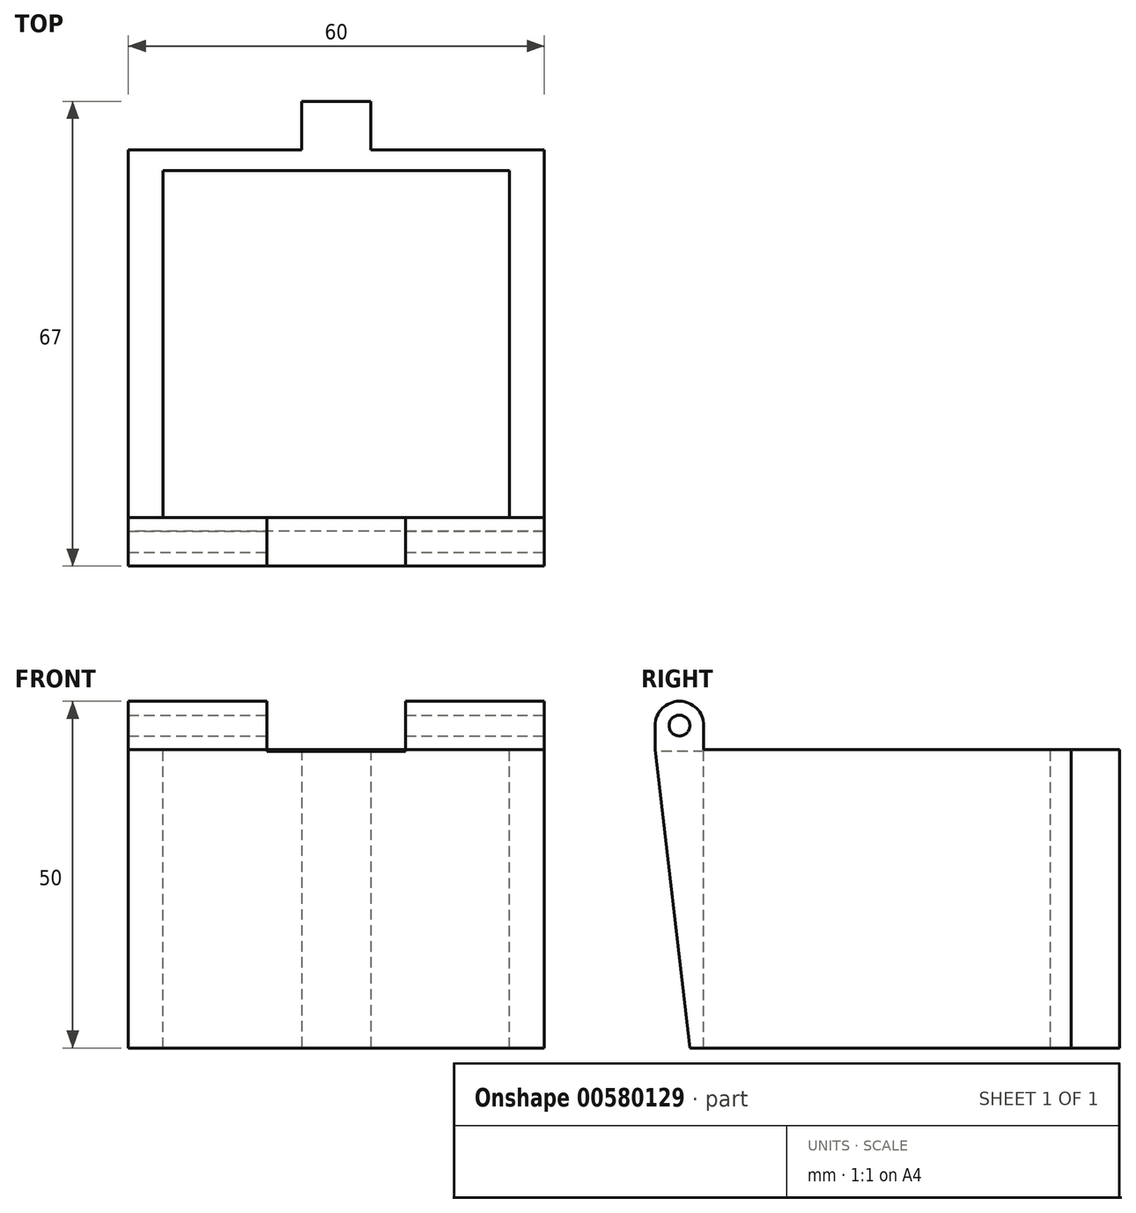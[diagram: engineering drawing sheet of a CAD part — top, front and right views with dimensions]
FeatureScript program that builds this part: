
annotation { "Feature Type Name" : "Feature", "Feature Type Description" : "" }
export const myFeature = defineFeature(function(context is Context, id is Id, definition is map)
    precondition{}
    {
        {
            var Q0;
            Q0=qCreatedBy(makeId("Top.planeOp"),FACE);
            var sketch = newSketch(context, id + "F0", { "sketchPlane" : qUnion([Q0])});
            skLineSegment(sketch, "E0.bottom", {"start": v(-57.5, 32) * mm, "end": v(57.5, 32) * mm});
            skLineSegment(sketch, "E0.top", {"start": v(-57.5, -35) * mm, "end": v(57.5, -35) * mm});
            skLineSegment(sketch, "E0.left", {"start": v(-57.5, 32) * mm, "end": v(-57.5, -35) * mm});
            skLineSegment(sketch, "E0.right", {"start": v(57.5, 32) * mm, "end": v(57.5, -35) * mm});
            skLineSegment(sketch, "E1.bottom", {"start": v(-52.5, 25) * mm, "end": v(-2.5, 25) * mm});
            skLineSegment(sketch, "E1.top", {"start": v(-52.5, -25) * mm, "end": v(-2.5, -25) * mm});
            skLineSegment(sketch, "E1.left", {"start": v(-52.5, 25) * mm, "end": v(-52.5, -25) * mm});
            skLineSegment(sketch, "E1.right", {"start": v(-2.5, 25) * mm, "end": v(-2.5, -25) * mm});
            skLineSegment(sketch, "E2.bottom", {"start": v(2.5, 25) * mm, "end": v(52.5, 25) * mm});
            skLineSegment(sketch, "E2.top", {"start": v(2.5, -25) * mm, "end": v(52.5, -25) * mm});
            skLineSegment(sketch, "E2.left", {"start": v(2.5, 25) * mm, "end": v(2.5, -25) * mm});
            skLineSegment(sketch, "E2.right", {"start": v(52.5, 25) * mm, "end": v(52.5, -25) * mm});
            skSolve(sketch);
        }
        {
            var Q0;
            Q0=makeQuery(id+"F0.imprint","IMPRINT",FACE,{"disambiguationData":[TD([[makeQuery(id+"F0.imprint","IMPRINT",EDGE,{"derivedFrom":sQuery(id+"F0.wireOp",EDGE,"E0.bottom")}),-1.0]])]});
            extrude(context, id + "F1", {"entities" : qUnion([Q0]), "depth" : 50 * mm, "offsetDistance" : 25 * mm});
        }
        {
            var Q0;
            Q0=makeQuery(id+"F1.opExtrude","CAP_EDGE",EDGE,{"disambiguationData":[OSD([sQuery(id+"F0.wireOp",EDGE,"E0.bottom")])],"isStart":true});
            fillet(context, id + "F2", {"entities" : qUnion([Q0]), "radius" : 3.5 * mm, "tangentPropagation" : true, "allowEdgeOverflow" : false});
        }
        {
            var Q0;
            Q0=makeQuery(id+"F1.opExtrude","CAP_EDGE",EDGE,{"disambiguationData":[OSD([sQuery(id+"F0.wireOp",EDGE,"E1.bottom")])],"isStart":true});
            var Q1;
            Q1=makeQuery(id+"F1.opExtrude","CAP_EDGE",EDGE,{"disambiguationData":[OSD([sQuery(id+"F0.wireOp",EDGE,"E2.bottom")])],"isStart":true});
            fillet(context, id + "F3", {"entities" : qUnion([Q0, Q1]), "radius" : 3.5 * mm, "tangentPropagation" : true, "allowEdgeOverflow" : false});
        }
        {
            var Q0;
            Q0=makeQuery(id+"F1.opExtrude","SWEPT_FACE",FACE,{"disambiguationData":[OSD([sQuery(id+"F0.wireOp",EDGE,"E0.right")])]});
            var sketch = newSketch(context, id + "F4", { "sketchPlane" : qUnion([Q0])});
            skPoint(sketch, "E3", {"position": v(28.5, 3.5) * mm});
            skSolve(sketch);
        }
        {
            var Q0;
            Q0=sQuery(id+"F4.wireOp",VERTEX,"E3");
            var Q1;
            Q1=makeQuery(id+"F1.opExtrude","SWEPT_BODY",BODY,{"disambiguationData":[OSD([sQuery(id+"F0.wireOp",EDGE,"E0.bottom"),sQuery(id+"F0.wireOp",EDGE,"E0.top"),sQuery(id+"F0.wireOp",EDGE,"E0.left"),sQuery(id+"F0.wireOp",EDGE,"E0.right"),sQuery(id+"F0.wireOp",EDGE,"E1.bottom"),sQuery(id+"F0.wireOp",EDGE,"E1.top"),sQuery(id+"F0.wireOp",EDGE,"E1.left"),sQuery(id+"F0.wireOp",EDGE,"E1.right"),sQuery(id+"F0.wireOp",EDGE,"E2.bottom"),sQuery(id+"F0.wireOp",EDGE,"E2.top"),sQuery(id+"F0.wireOp",EDGE,"E2.left"),sQuery(id+"F0.wireOp",EDGE,"E2.right")])]});
            hole(context, id + "F5", {"style" : HoleStyle.SIMPLE, "endStyle" : HoleEndStyle.THROUGH, "holeDiameter" : 3 * mm, "isTappedThrough" : true, "tappedDepth" : 12 * mm, "tapClearance" : 3, "locations" : qUnion([Q0]), "scope" : qUnion([Q1])});
        }
        {
            var Q0;
            Q0=makeQuery(id+"F1.opExtrude","CAP_FACE",FACE,{"disambiguationData":[OSD([sQuery(id+"F0.wireOp",EDGE,"E0.bottom"),sQuery(id+"F0.wireOp",EDGE,"E0.top"),sQuery(id+"F0.wireOp",EDGE,"E0.left"),sQuery(id+"F0.wireOp",EDGE,"E0.right"),sQuery(id+"F0.wireOp",EDGE,"E1.bottom"),sQuery(id+"F0.wireOp",EDGE,"E1.top"),sQuery(id+"F0.wireOp",EDGE,"E1.left"),sQuery(id+"F0.wireOp",EDGE,"E1.right"),sQuery(id+"F0.wireOp",EDGE,"E2.bottom"),sQuery(id+"F0.wireOp",EDGE,"E2.top"),sQuery(id+"F0.wireOp",EDGE,"E2.left"),sQuery(id+"F0.wireOp",EDGE,"E2.right")])],"isStart":true});
            var sketch = newSketch(context, id + "F6", { "sketchPlane" : qUnion([Q0])});
            skLineSegment(sketch, "E4.bottom", {"start": v(-37.5, -25) * mm, "end": v(-17.5, -25) * mm});
            skLineSegment(sketch, "E4.top", {"start": v(-37.5, -35) * mm, "end": v(-17.5, -35) * mm});
            skLineSegment(sketch, "E4.left", {"start": v(-37.5, -25) * mm, "end": v(-37.5, -35) * mm});
            skLineSegment(sketch, "E4.right", {"start": v(-17.5, -25) * mm, "end": v(-17.5, -35) * mm});
            skLineSegment(sketch, "E5.1.0.0", {"start": v(37.5, -25) * mm, "end": v(37.5, -35) * mm});
            skLineSegment(sketch, "E5.1.0.1", {"start": v(17.5, -25) * mm, "end": v(17.5, -35) * mm});
            skLineSegment(sketch, "E5.1.0.2", {"start": v(17.5, -25) * mm, "end": v(37.5, -25) * mm});
            skLineSegment(sketch, "E5.1.0.3", {"start": v(17.5, -35) * mm, "end": v(37.5, -35) * mm});
            skLineSegment(sketch, "E5.direction1", {"start": v(-37.5, -35) * mm, "end": v(17.5, -35) * mm, "construction": true});
            skSolve(sketch);
        }
        {
            var Q0;
            Q0=makeQuery(id+"F6.imprint","IMPRINT",FACE,{"disambiguationData":[TD([[makeQuery(id+"F6.imprint","IMPRINT",EDGE,{"derivedFrom":sQuery(id+"F6.wireOp",EDGE,"E4.bottom")}),-1.0]])]});
            var Q1;
            Q1=makeQuery(id+"F6.imprint","IMPRINT",FACE,{"disambiguationData":[TD([[makeQuery(id+"F6.imprint","IMPRINT",EDGE,{"derivedFrom":sQuery(id+"F6.wireOp",EDGE,"E5.1.0.0")}),-1.0]])]});
            extrude(context, id + "F7", {"entities" : qUnion([Q0, Q1]), "operationType" : NewBodyOperationType.REMOVE, "oppositeDirection" : true, "depth" : 7.2 * mm, "offsetDistance" : 25 * mm});
        }
        {
            var Q0;
            Q0=makeQuery(id+"F1.opExtrude","SWEPT_BODY",BODY,{"disambiguationData":[OSD([sQuery(id+"F0.wireOp",EDGE,"E0.bottom"),sQuery(id+"F0.wireOp",EDGE,"E0.top"),sQuery(id+"F0.wireOp",EDGE,"E0.left"),sQuery(id+"F0.wireOp",EDGE,"E0.right"),sQuery(id+"F0.wireOp",EDGE,"E1.bottom"),sQuery(id+"F0.wireOp",EDGE,"E1.top"),sQuery(id+"F0.wireOp",EDGE,"E1.left"),sQuery(id+"F0.wireOp",EDGE,"E1.right"),sQuery(id+"F0.wireOp",EDGE,"E2.bottom"),sQuery(id+"F0.wireOp",EDGE,"E2.top"),sQuery(id+"F0.wireOp",EDGE,"E2.left"),sQuery(id+"F0.wireOp",EDGE,"E2.right")])]});
            var Q1;
            {var subQ0=sQuery(id+"F0.wireOp",EDGE,"E0.top");Q1=makeQuery(id+"F380UEOeI2wlNUW_1.boolean.opBoolean","SPLIT",EDGE,{"disambiguationData":[TD([makeQuery(id+"F1.opExtrude","CAP_FACE",FACE,{"disambiguationData":[OSD([sQuery(id+"F0.wireOp",EDGE,"E0.bottom"),subQ0,sQuery(id+"F0.wireOp",EDGE,"E0.left"),sQuery(id+"F0.wireOp",EDGE,"E0.right"),sQuery(id+"F0.wireOp",EDGE,"E1.bottom"),sQuery(id+"F0.wireOp",EDGE,"E1.top"),sQuery(id+"F0.wireOp",EDGE,"E1.left"),sQuery(id+"F0.wireOp",EDGE,"E1.right"),sQuery(id+"F0.wireOp",EDGE,"E2.bottom"),sQuery(id+"F0.wireOp",EDGE,"E2.top"),sQuery(id+"F0.wireOp",EDGE,"E2.left"),sQuery(id+"F0.wireOp",EDGE,"E2.right")])],"isStart":true}),makeQuery(id+"F1.opExtrude","SWEPT_FACE",FACE,{"disambiguationData":[OSD([subQ0])]}),makeQuery(id+"F380UEOeI2wlNUW_1.opExtrude","SWEPT_FACE",FACE,{"disambiguationData":[OSD([sQuery(id+"FmOFaYkdt5LuX7B_1.wireOp",EDGE,"dlY3Qf5f-TCnb-0751-E5xM-8nm06BOcbGTX")])]}),makeQuery(id+"F380UEOeI2wlNUW_1.opExtrude","SWEPT_FACE",FACE,{"disambiguationData":[OSD([sQuery(id+"FmOFaYkdt5LuX7B_1.wireOp",EDGE,"d490bf6a-ab8b-4622-952c-336e381e35dc.1.0.0")])]})])],"derivedFrom":makeQuery(id+"F1.opExtrude","CAP_EDGE",EDGE,{"disambiguationData":[OSD([subQ0])],"isStart":true})});}
            transform(context, id + "F8", {"entities" : qUnion([Q0]), "transformType" : TransformType.ROTATION, "transformAxis" : qUnion([Q1]), "angle" : 180 * degree, "oppositeDirection" : true, "makeCopy" : false});
        }
        {
            var Q0;
            Q0=makeQuery(id+"F1.opExtrude","SWEPT_BODY",BODY,{"disambiguationData":[OSD([sQuery(id+"F0.wireOp",EDGE,"E0.bottom"),sQuery(id+"F0.wireOp",EDGE,"E0.top"),sQuery(id+"F0.wireOp",EDGE,"E0.left"),sQuery(id+"F0.wireOp",EDGE,"E0.right"),sQuery(id+"F0.wireOp",EDGE,"E1.bottom"),sQuery(id+"F0.wireOp",EDGE,"E1.top"),sQuery(id+"F0.wireOp",EDGE,"E1.left"),sQuery(id+"F0.wireOp",EDGE,"E1.right"),sQuery(id+"F0.wireOp",EDGE,"E2.bottom"),sQuery(id+"F0.wireOp",EDGE,"E2.top"),sQuery(id+"F0.wireOp",EDGE,"E2.left"),sQuery(id+"F0.wireOp",EDGE,"E2.right")])]});
            var Q1;
            Q1=qCreatedBy(makeId("Front.planeOp"),FACE);
            transform(context, id + "F9", {"entities" : qUnion([Q0]), "transformType" : TransformType.TRANSLATION_DISTANCE, "transformDirection" : qUnion([Q1]), "distance" : 70 * mm, "oppositeDirection" : true, "makeCopy" : false});
        }
        {
            var Q0;
            Q0=makeQuery(id+"F1.opExtrude","SWEPT_BODY",BODY,{"disambiguationData":[OSD([sQuery(id+"F0.wireOp",EDGE,"E0.bottom"),sQuery(id+"F0.wireOp",EDGE,"E0.top"),sQuery(id+"F0.wireOp",EDGE,"E0.left"),sQuery(id+"F0.wireOp",EDGE,"E0.right"),sQuery(id+"F0.wireOp",EDGE,"E1.bottom"),sQuery(id+"F0.wireOp",EDGE,"E1.top"),sQuery(id+"F0.wireOp",EDGE,"E1.left"),sQuery(id+"F0.wireOp",EDGE,"E1.right"),sQuery(id+"F0.wireOp",EDGE,"E2.bottom"),sQuery(id+"F0.wireOp",EDGE,"E2.top"),sQuery(id+"F0.wireOp",EDGE,"E2.left"),sQuery(id+"F0.wireOp",EDGE,"E2.right")])]});
            var Q1;
            Q1=qCreatedBy(makeId("Top.planeOp"),FACE);
            transform(context, id + "F10", {"entities" : qUnion([Q0]), "transformType" : TransformType.TRANSLATION_DISTANCE, "transformDirection" : qUnion([Q1]), "distance" : 50 * mm, "makeCopy" : false});
        }
        {
            var Q0;
            Q0=makeQuery(id+"F1.opExtrude","SWEPT_FACE",FACE,{"disambiguationData":[OSD([sQuery(id+"F0.wireOp",EDGE,"E0.left")])]});
            var sketch = newSketch(context, id + "F11", { "sketchPlane" : qUnion([Q0])});
            skLineSegment(sketch, "E6", {"start": v(32, 43) * mm, "end": v(27, 0) * mm});
            skLineSegment(sketch, "E7", {"start": v(27, 0) * mm, "end": v(32, 0) * mm});
            skLineSegment(sketch, "E8", {"start": v(32, 0) * mm, "end": v(32, 43) * mm});
            skSolve(sketch);
        }
        {
            var Q0;
            Q0=makeQuery(id+"F11.imprint","IMPRINT",FACE,{"disambiguationData":[TD([[makeQuery(id+"F11.imprint","IMPRINT",EDGE,{"derivedFrom":sQuery(id+"F11.wireOp",EDGE,"E6")}),1.0]])]});
            extrude(context, id + "F12", {"entities" : qUnion([Q0]), "operationType" : NewBodyOperationType.REMOVE, "endBound" : BoundingType.UP_TO_NEXT, "oppositeDirection" : true, "depth" : 25 * mm, "offsetDistance" : 25 * mm});
        }
        {
            var Q0;
            Q0=makeQuery(id+"F1.opExtrude","SWEPT_FACE",FACE,{"disambiguationData":[OSD([sQuery(id+"F0.wireOp",EDGE,"E0.top")])]});
            var sketch = newSketch(context, id + "F13", { "sketchPlane" : qUnion([Q0])});
            skLineSegment(sketch, "E9.top", {"start": v(-57.5, 0) * mm, "end": v(-32.5, 0) * mm});
            skLineSegment(sketch, "E9.left", {"start": v(-57.5, 50) * mm, "end": v(-57.5, 0) * mm});
            skLineSegment(sketch, "E9.right", {"start": v(-32.5, 43) * mm, "end": v(-32.5, 0) * mm});
            skLineSegment(sketch, "E10.top", {"start": v(-22.5, 0) * mm, "end": v(22.5, 0) * mm});
            skLineSegment(sketch, "E10.left", {"start": v(-22.5, 43) * mm, "end": v(-22.5, 0) * mm});
            skLineSegment(sketch, "E10.right", {"start": v(22.5, 43) * mm, "end": v(22.5, 0) * mm});
            skLineSegment(sketch, "E11.top", {"start": v(32.5, 0) * mm, "end": v(57.5, 0) * mm});
            skLineSegment(sketch, "E11.left", {"start": v(32.5, 43) * mm, "end": v(32.5, 0) * mm});
            skLineSegment(sketch, "E11.right", {"start": v(57.5, 50) * mm, "end": v(57.5, 0) * mm});
            skLineSegment(sketch, "E12.top", {"start": v(-32.5, 43) * mm, "end": v(-22.5, 43) * mm});
            skLineSegment(sketch, "E13.top", {"start": v(22.5, 43) * mm, "end": v(32.5, 43) * mm});
            skSolve(sketch);
        }
        {
            var Q0;
            Q0=makeQuery(id+"F13.imprint","IMPRINT",FACE,{"disambiguationData":[TD([[makeQuery(id+"F13.imprint","IMPRINT",EDGE,{"derivedFrom":sQuery(id+"F13.wireOp",EDGE,"E9.top")}),-1.0]])]});
            extrude(context, id + "F14", {"entities" : qUnion([Q0]), "operationType" : NewBodyOperationType.REMOVE, "oppositeDirection" : true, "depth" : 7 * mm, "offsetDistance" : 25 * mm});
        }
        {
            var Q0;
            Q0=makeQuery(id+"F1.opExtrude","SWEPT_FACE",FACE,{"disambiguationData":[OSD([sQuery(id+"F0.wireOp",EDGE,"E2.left")])]});
            var sketch = newSketch(context, id + "F15", { "sketchPlane" : qUnion([Q0])});
            skLineSegment(sketch, "E14.bottom", {"start": v(-43.74, 56.73) * mm, "end": v(49.95, 56.73) * mm});
            skLineSegment(sketch, "E14.top", {"start": v(-43.74, -7.86) * mm, "end": v(49.95, -7.86) * mm});
            skLineSegment(sketch, "E14.left", {"start": v(-43.74, 56.73) * mm, "end": v(-43.74, -7.86) * mm});
            skLineSegment(sketch, "E14.right", {"start": v(49.95, 56.73) * mm, "end": v(49.95, -7.86) * mm});
            skSolve(sketch);
        }
        {
            var Q0;
            Q0 = qSketchRegion(id + "F15", true);
            extrude(context, id + "F16", {"entities" : qUnion([Q0]), "operationType" : NewBodyOperationType.REMOVE, "depth" : 70 * mm, "offsetDistance" : 25 * mm});
        }
        {
            var Q0;
            Q0=makeQuery(id+"F16.boolean.opBoolean","MERGE",FACE,{"derivedFrom":[makeQuery(id+"F1.opExtrude","SWEPT_FACE",FACE,{"disambiguationData":[OSD([sQuery(id+"F0.wireOp",EDGE,"E2.left")])]}),makeQuery(id+"F16.opExtrude","CAP_FACE",FACE,{"disambiguationData":[OSD([sQuery(id+"F15.wireOp",EDGE,"E14.bottom"),sQuery(id+"F15.wireOp",EDGE,"E14.top"),sQuery(id+"F15.wireOp",EDGE,"E14.left"),sQuery(id+"F15.wireOp",EDGE,"E14.right")])],"isStart":true})]});
            var sketch = newSketch(context, id + "F17", { "sketchPlane" : qUnion([Q0])});
            skLineSegment(sketch, "E15.bottom", {"start": v(28, 50) * mm, "end": v(-28.5, 50) * mm});
            skLineSegment(sketch, "E15.top", {"start": v(28, 43) * mm, "end": v(-25, 43) * mm});
            skLineSegment(sketch, "E15.left", {"start": v(28, 50) * mm, "end": v(28, 43) * mm});
            skLineSegment(sketch, "E15.right", {"start": v(-25, 46.5) * mm, "end": v(-25, 43) * mm});
            skArc(sketch, "E16", {"start": v(-25, 46.5) * mm, "mid": v(-26.03, 48.97) * mm, "end": v(-28.5, 50) * mm});
            skSolve(sketch);
        }
        {
            var Q0;
            Q0 = qSketchRegion(id + "F17", true);
            extrude(context, id + "F18", {"entities" : qUnion([Q0]), "operationType" : NewBodyOperationType.REMOVE, "oppositeDirection" : true, "depth" : 100 * mm, "offsetDistance" : 25 * mm});
        }
    });
